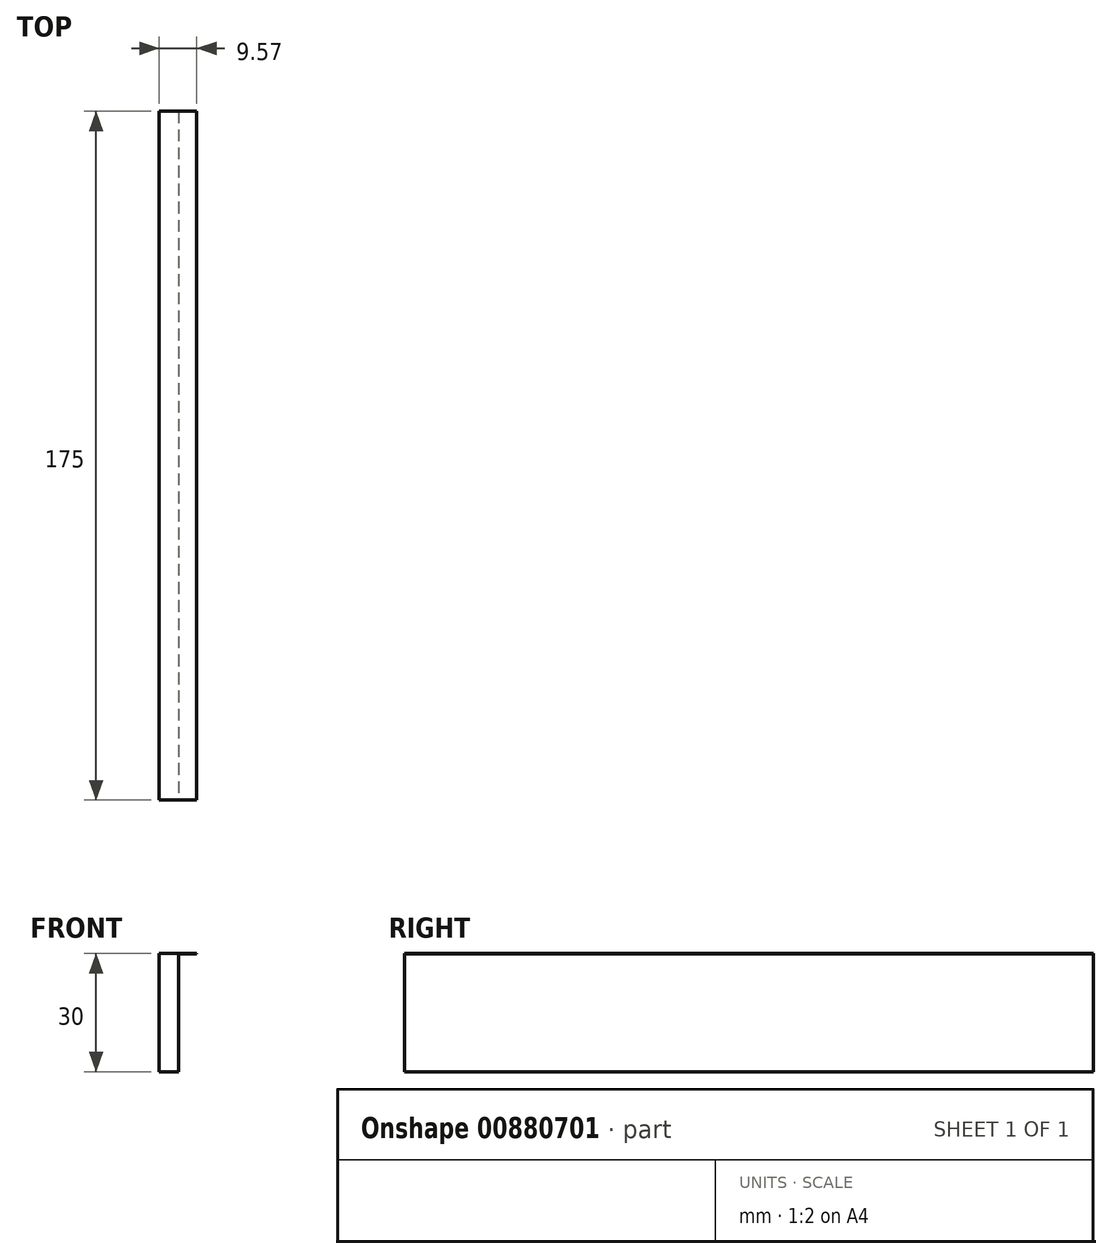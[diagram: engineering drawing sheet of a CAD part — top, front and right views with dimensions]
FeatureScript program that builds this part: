
annotation { "Feature Type Name" : "Feature", "Feature Type Description" : "" }
export const myFeature = defineFeature(function(context is Context, id is Id, definition is map)
    precondition{}
    {
        {
            var Q0;
            Q0=qCreatedBy(makeId("Front.planeOp"),FACE);
            var sketch = newSketch(context, id + "F0", { "sketchPlane" : qUnion([Q0])});
            skLineSegment(sketch, "E0.bottom", {"start": v(-10.77, 17.51) * mm, "end": v(-5.77, 17.51) * mm});
            skLineSegment(sketch, "E0.top", {"start": v(-10.77, -12.49) * mm, "end": v(-5.77, -12.49) * mm});
            skLineSegment(sketch, "E0.left", {"start": v(-10.77, 17.51) * mm, "end": v(-10.77, -12.49) * mm});
            skLineSegment(sketch, "E0.right", {"start": v(-5.77, 17.5) * mm, "end": v(-5.77, -12.49) * mm});
            skLineSegment(sketch, "E1.bottom", {"start": v(-10.77, 17.51) * mm, "end": v(-1.2, 17.51) * mm});
            skLineSegment(sketch, "E1.top", {"start": v(-5.77, 17.5) * mm, "end": v(-1.2, 17.5) * mm});
            skLineSegment(sketch, "E1.left", {"start": v(-10.77, 17.51) * mm, "end": v(-10.77, 17.5) * mm});
            skLineSegment(sketch, "E1.right", {"start": v(-1.2, 17.51) * mm, "end": v(-1.2, 17.5) * mm});
            skSolve(sketch);
        }
        {
            var Q0;
            Q0=makeQuery(id+"F0.imprint","IMPRINT",FACE,{"disambiguationData":[TD([[makeQuery(id+"F0.imprint","IMPRINT",EDGE,{"derivedFrom":sQuery(id+"F0.wireOp",EDGE,"E0.top")}),1.0]])]});
            extrude(context, id + "F1", {"entities" : qUnion([Q0]), "oppositeDirection" : true, "depth" : 175 * mm, "offsetDistance" : 25 * mm});
        }
    });
